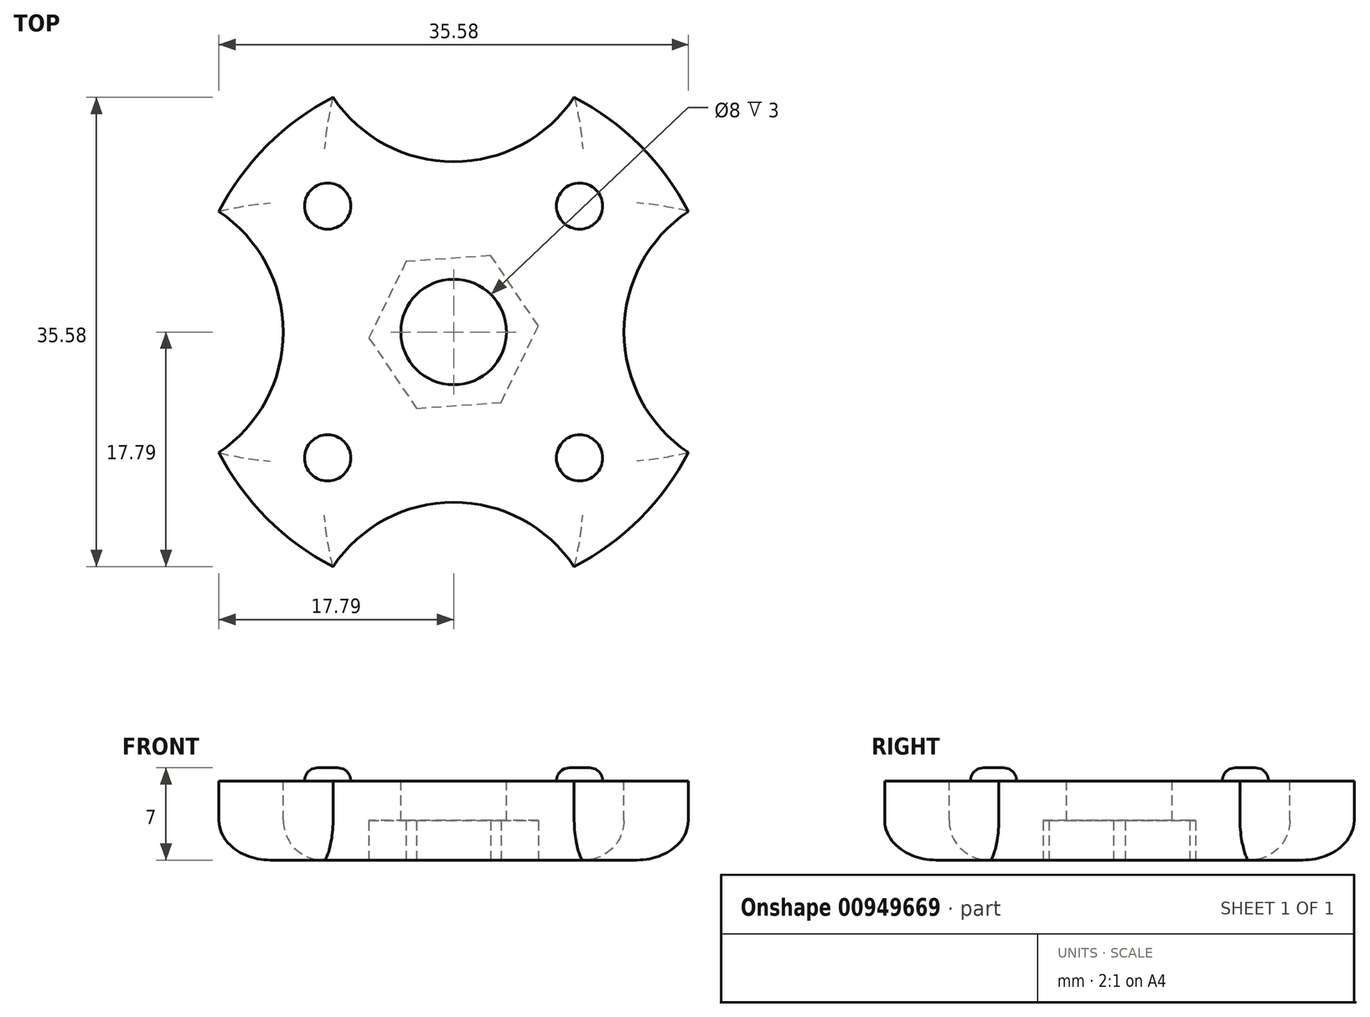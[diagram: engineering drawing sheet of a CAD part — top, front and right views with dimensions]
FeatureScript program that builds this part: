
annotation { "Feature Type Name" : "Feature", "Feature Type Description" : "" }
export const myFeature = defineFeature(function(context is Context, id is Id, definition is map)
    precondition{}
    {
        {
            var Q0;
            Q0=qCreatedBy(makeId("Top.planeOp"),FACE);
            var sketch = newSketch(context, id + "F0", { "sketchPlane" : qUnion([Q0])});
            skCircle(sketch, "E0", {"center": v(0, 0) * mm, "radius": 20 * mm});
            skCircle(sketch, "E1", {"center": v(0, 0) * mm, "radius": 13.5 * mm, "construction": true});
            skCircle(sketch, "E2", {"center": v(0, 13.5) * mm, "radius": 1.75 * mm});
            skCircle(sketch, "E3.1.0", {"center": v(-13.5, 0) * mm, "radius": 1.75 * mm});
            skCircle(sketch, "E3.2.0", {"center": v(0, -13.5) * mm, "radius": 1.75 * mm});
            skCircle(sketch, "E3.3.0", {"center": v(13.5, 0) * mm, "radius": 1.75 * mm});
            skCircle(sketch, "E4", {"center": v(0, 0) * mm, "radius": 4 * mm});
            skSolve(sketch);
        }
        {
            var Q0;
            Q0=makeQuery(id+"F0.imprint","IMPRINT",FACE,{"disambiguationData":[TD([[makeQuery(id+"F0.imprint","IMPRINT",EDGE,{"derivedFrom":sQuery(id+"F0.wireOp",EDGE,"E0")}),1.0]])]});
            extrude(context, id + "F1", {"entities" : qUnion([Q0]), "oppositeDirection" : true, "depth" : 6 * mm, "offsetDistance" : 25 * mm});
        }
        {
            var Q0;
            Q0=makeQuery(id+"F0.imprint","IMPRINT",FACE,{"disambiguationData":[TD([[makeQuery(id+"F0.imprint","IMPRINT",EDGE,{"derivedFrom":sQuery(id+"F0.wireOp",EDGE,"E3.1.0")}),1.0]])]});
            var Q1;
            Q1=makeQuery(id+"F0.imprint","IMPRINT",FACE,{"disambiguationData":[TD([[makeQuery(id+"F0.imprint","IMPRINT",EDGE,{"derivedFrom":sQuery(id+"F0.wireOp",EDGE,"E2")}),1.0]])]});
            var Q2;
            Q2=makeQuery(id+"F0.imprint","IMPRINT",FACE,{"disambiguationData":[TD([[makeQuery(id+"F0.imprint","IMPRINT",EDGE,{"derivedFrom":sQuery(id+"F0.wireOp",EDGE,"E3.3.0")}),1.0]])]});
            var Q3;
            Q3=makeQuery(id+"F0.imprint","IMPRINT",FACE,{"disambiguationData":[TD([[makeQuery(id+"F0.imprint","IMPRINT",EDGE,{"derivedFrom":sQuery(id+"F0.wireOp",EDGE,"E3.2.0")}),1.0]])]});
            extrude(context, id + "F2", {"entities" : qUnion([Q0, Q1, Q2, Q3]), "depth" : 1 * mm, "offsetDistance" : 25 * mm});
        }
        {
            var Q0;
            Q0=makeQuery(id+"F2.opExtrude","CAP_FACE",FACE,{"disambiguationData":[OSD([sQuery(id+"F0.wireOp",EDGE,"E3.2.0")])],"isStart":true});
            var Q1;
            Q1=makeQuery(id+"F1.opExtrude","CAP_FACE",FACE,{"disambiguationData":[OSD([sQuery(id+"F0.wireOp",EDGE,"E0"),sQuery(id+"F0.wireOp",EDGE,"E2"),sQuery(id+"F0.wireOp",EDGE,"E3.1.0"),sQuery(id+"F0.wireOp",EDGE,"E3.2.0"),sQuery(id+"F0.wireOp",EDGE,"E3.3.0"),sQuery(id+"F0.wireOp",EDGE,"E4")])],"isStart":false});
            extrude(context, id + "F3", {"entities" : qUnion([Q0]), "operationType" : NewBodyOperationType.ADD, "endBound" : BoundingType.UP_TO_SURFACE, "depth" : 25 * mm, "endBoundEntityFace" : qUnion([Q1]), "offsetDistance" : 25 * mm});
        }
        {
            var Q0;
            Q0=makeQuery(id+"F2.opExtrude","CAP_FACE",FACE,{"disambiguationData":[OSD([sQuery(id+"F0.wireOp",EDGE,"E3.3.0")])],"isStart":true});
            var Q1;
            {var subQ0=sQuery(id+"F0.wireOp",EDGE,"E3.2.0");Q1=makeQuery(id+"F3.boolean.opBoolean","MERGE",FACE,{"derivedFrom":[makeQuery(id+"F1.opExtrude","CAP_FACE",FACE,{"disambiguationData":[OSD([sQuery(id+"F0.wireOp",EDGE,"E0"),sQuery(id+"F0.wireOp",EDGE,"E2"),sQuery(id+"F0.wireOp",EDGE,"E3.1.0"),subQ0,sQuery(id+"F0.wireOp",EDGE,"E3.3.0"),sQuery(id+"F0.wireOp",EDGE,"E4")])],"isStart":false}),makeQuery(id+"F3.opExtrude","CAP_FACE",FACE,{"disambiguationData":[OSD([subQ0])],"isStart":false})]});}
            extrude(context, id + "F4", {"entities" : qUnion([Q0]), "operationType" : NewBodyOperationType.ADD, "endBound" : BoundingType.UP_TO_SURFACE, "depth" : 25 * mm, "endBoundEntityFace" : qUnion([Q1]), "offsetDistance" : 25 * mm});
        }
        {
            var Q0;
            Q0=makeQuery(id+"F2.opExtrude","CAP_FACE",FACE,{"disambiguationData":[OSD([sQuery(id+"F0.wireOp",EDGE,"E3.1.0")])],"isStart":true});
            var Q1;
            {var subQ0=sQuery(id+"F0.wireOp",EDGE,"E3.3.0");var subQ1=sQuery(id+"F0.wireOp",EDGE,"E3.2.0");Q1=makeQuery(id+"F4.boolean.opBoolean","MERGE",FACE,{"derivedFrom":[makeQuery(id+"F3.boolean.opBoolean","MERGE",FACE,{"derivedFrom":[makeQuery(id+"F1.opExtrude","CAP_FACE",FACE,{"disambiguationData":[OSD([sQuery(id+"F0.wireOp",EDGE,"E0"),sQuery(id+"F0.wireOp",EDGE,"E2"),sQuery(id+"F0.wireOp",EDGE,"E3.1.0"),subQ1,subQ0,sQuery(id+"F0.wireOp",EDGE,"E4")])],"isStart":false}),makeQuery(id+"F3.opExtrude","CAP_FACE",FACE,{"disambiguationData":[OSD([subQ1])],"isStart":false})]}),makeQuery(id+"F4.opExtrude","CAP_FACE",FACE,{"disambiguationData":[OSD([subQ0])],"isStart":false})]});}
            extrude(context, id + "F5", {"entities" : qUnion([Q0]), "operationType" : NewBodyOperationType.ADD, "endBound" : BoundingType.UP_TO_SURFACE, "depth" : 25 * mm, "endBoundEntityFace" : qUnion([Q1]), "offsetDistance" : 25 * mm});
        }
        {
            var Q0;
            Q0=makeQuery(id+"F2.opExtrude","CAP_FACE",FACE,{"disambiguationData":[OSD([sQuery(id+"F0.wireOp",EDGE,"E2")])],"isStart":true});
            var Q1;
            {var subQ0=sQuery(id+"F0.wireOp",EDGE,"E3.1.0");var subQ1=sQuery(id+"F0.wireOp",EDGE,"E3.3.0");var subQ2=sQuery(id+"F0.wireOp",EDGE,"E3.2.0");Q1=makeQuery(id+"F5.boolean.opBoolean","MERGE",FACE,{"derivedFrom":[makeQuery(id+"F4.boolean.opBoolean","MERGE",FACE,{"derivedFrom":[makeQuery(id+"F3.boolean.opBoolean","MERGE",FACE,{"derivedFrom":[makeQuery(id+"F1.opExtrude","CAP_FACE",FACE,{"disambiguationData":[OSD([sQuery(id+"F0.wireOp",EDGE,"E0"),sQuery(id+"F0.wireOp",EDGE,"E2"),subQ0,subQ2,subQ1,sQuery(id+"F0.wireOp",EDGE,"E4")])],"isStart":false}),makeQuery(id+"F3.opExtrude","CAP_FACE",FACE,{"disambiguationData":[OSD([subQ2])],"isStart":false})]}),makeQuery(id+"F4.opExtrude","CAP_FACE",FACE,{"disambiguationData":[OSD([subQ1])],"isStart":false})]}),makeQuery(id+"F5.opExtrude","CAP_FACE",FACE,{"disambiguationData":[OSD([subQ0])],"isStart":false})]});}
            extrude(context, id + "F6", {"entities" : qUnion([Q0]), "operationType" : NewBodyOperationType.ADD, "endBound" : BoundingType.UP_TO_SURFACE, "depth" : 25 * mm, "endBoundEntityFace" : qUnion([Q1]), "offsetDistance" : 25 * mm});
        }
        {
            var Q0;
            Q0=makeQuery(id+"F2.opExtrude","CAP_EDGE",EDGE,{"disambiguationData":[OSD([sQuery(id+"F0.wireOp",EDGE,"E3.3.0")])],"isStart":false});
            var Q1;
            Q1=makeQuery(id+"F2.opExtrude","CAP_EDGE",EDGE,{"disambiguationData":[OSD([sQuery(id+"F0.wireOp",EDGE,"E3.2.0")])],"isStart":false});
            var Q2;
            Q2=makeQuery(id+"F2.opExtrude","CAP_EDGE",EDGE,{"disambiguationData":[OSD([sQuery(id+"F0.wireOp",EDGE,"E2")])],"isStart":false});
            var Q3;
            Q3=makeQuery(id+"F2.opExtrude","CAP_EDGE",EDGE,{"disambiguationData":[OSD([sQuery(id+"F0.wireOp",EDGE,"E3.1.0")])],"isStart":false});
            fillet(context, id + "F7", {"entities" : qUnion([Q0, Q1, Q2, Q3]), "radius" : 1 * mm, "tangentPropagation" : true, "allowEdgeOverflow" : false});
        }
        {
            var Q0;
            {var subQ0=sQuery(id+"F0.wireOp",EDGE,"E2");var subQ1=sQuery(id+"F0.wireOp",EDGE,"E3.1.0");var subQ2=sQuery(id+"F0.wireOp",EDGE,"E3.3.0");var subQ3=sQuery(id+"F0.wireOp",EDGE,"E3.2.0");Q0=makeQuery(id+"F6.boolean.opBoolean","MERGE",FACE,{"derivedFrom":[makeQuery(id+"F5.boolean.opBoolean","MERGE",FACE,{"derivedFrom":[makeQuery(id+"F4.boolean.opBoolean","MERGE",FACE,{"derivedFrom":[makeQuery(id+"F3.boolean.opBoolean","MERGE",FACE,{"derivedFrom":[makeQuery(id+"F1.opExtrude","CAP_FACE",FACE,{"disambiguationData":[OSD([sQuery(id+"F0.wireOp",EDGE,"E0"),subQ0,subQ1,subQ3,subQ2,sQuery(id+"F0.wireOp",EDGE,"E4")])],"isStart":false}),makeQuery(id+"F3.opExtrude","CAP_FACE",FACE,{"disambiguationData":[OSD([subQ3])],"isStart":false})]}),makeQuery(id+"F4.opExtrude","CAP_FACE",FACE,{"disambiguationData":[OSD([subQ2])],"isStart":false})]}),makeQuery(id+"F5.opExtrude","CAP_FACE",FACE,{"disambiguationData":[OSD([subQ1])],"isStart":false})]}),makeQuery(id+"F6.opExtrude","CAP_FACE",FACE,{"disambiguationData":[OSD([subQ0])],"isStart":false})]});}
            var sketch = newSketch(context, id + "F8", { "sketchPlane" : qUnion([Q0])});
            skCircle(sketch, "E5.cCircle", {"center": v(0, 0) * mm, "radius": 6.44 * mm, "construction": true});
            skLineSegment(sketch, "E5.0", {"start": v(4.22, -4.86) * mm, "end": v(-2.1, -6.09) * mm});
            skLineSegment(sketch, "E5.1", {"start": v(-2.1, -6.09) * mm, "end": v(-6.32, -1.23) * mm});
            skLineSegment(sketch, "E5.2", {"start": v(-6.32, -1.23) * mm, "end": v(-4.22, 4.86) * mm});
            skLineSegment(sketch, "E5.3", {"start": v(-4.22, 4.86) * mm, "end": v(2.1, 6.09) * mm});
            skLineSegment(sketch, "E5.4", {"start": v(2.1, 6.09) * mm, "end": v(6.32, 1.23) * mm});
            skLineSegment(sketch, "E5.5", {"start": v(6.32, 1.23) * mm, "end": v(4.22, -4.86) * mm});
            skSolve(sketch);
        }
        {
            var Q0;
            Q0=makeQuery(id+"F8.imprint","IMPRINT",FACE,{"disambiguationData":[TD([[makeQuery(id+"F8.imprint","IMPRINT",EDGE,{"derivedFrom":sQuery(id+"F8.wireOp",EDGE,"E5.0")}),-1.0]])]});
            extrude(context, id + "F9", {"entities" : qUnion([Q0]), "operationType" : NewBodyOperationType.REMOVE, "oppositeDirection" : true, "depth" : 3 * mm, "offsetDistance" : 25 * mm});
        }
        {
            var Q0;
            Q0=makeQuery(id+"F1.opExtrude","SWEPT_BODY",BODY,{"disambiguationData":[OSD([sQuery(id+"F0.wireOp",EDGE,"E0"),sQuery(id+"F0.wireOp",EDGE,"E2"),sQuery(id+"F0.wireOp",EDGE,"E3.1.0"),sQuery(id+"F0.wireOp",EDGE,"E3.2.0"),sQuery(id+"F0.wireOp",EDGE,"E3.3.0"),sQuery(id+"F0.wireOp",EDGE,"E4")])]});
            var Q1;
            Q1=makeQuery(id+"F1.opExtrude","SWEPT_FACE",FACE,{"disambiguationData":[OSD([sQuery(id+"F0.wireOp",EDGE,"E4")])]});
            transform(context, id + "F10", {"entities" : qUnion([Q0]), "transformType" : TransformType.ROTATION, "transformAxis" : qUnion([Q1]), "angle" : 45 * degree, "makeCopy" : false});
        }
        {
            var Q0;
            Q0=makeQuery(id+"F1.opExtrude","CAP_FACE",FACE,{"disambiguationData":[OSD([sQuery(id+"F0.wireOp",EDGE,"E0"),sQuery(id+"F0.wireOp",EDGE,"E2"),sQuery(id+"F0.wireOp",EDGE,"E3.1.0"),sQuery(id+"F0.wireOp",EDGE,"E3.2.0"),sQuery(id+"F0.wireOp",EDGE,"E3.3.0"),sQuery(id+"F0.wireOp",EDGE,"E4")])],"isStart":true});
            var sketch = newSketch(context, id + "F11", { "sketchPlane" : qUnion([Q0])});
            skCircle(sketch, "E6", {"center": v(0, 0) * mm, "radius": 23.91 * mm, "construction": true});
            skCircle(sketch, "E7", {"center": v(0, 23.91) * mm, "radius": 11 * mm});
            skCircle(sketch, "E8.1.0", {"center": v(-23.91, 0) * mm, "radius": 11 * mm});
            skCircle(sketch, "E8.2.0", {"center": v(0, -23.91) * mm, "radius": 11 * mm});
            skCircle(sketch, "E8.3.0", {"center": v(23.91, 0) * mm, "radius": 11 * mm});
            skSolve(sketch);
        }
        {
            var Q0;
            {var subQ0=sQuery(id+"F11.wireOp",EDGE,"E7");var subQ1=makeQuery(id+"F1.opExtrude","CAP_EDGE",EDGE,{"disambiguationData":[OSD([sQuery(id+"F0.wireOp",EDGE,"E0")])],"isStart":true});var subQ2=makeQuery(id+"F11.imprint","INTERSECT",VERTEX,{"disambiguationData":[OD(0.0)],"derivedFrom":[subQ1,subQ0]});Q0=makeQuery(id+"F11.imprint","IMPRINT",FACE,{"disambiguationData":[TD([[makeQuery(id+"F11.imprint","IMPRINT",EDGE,{"disambiguationData":[TD([[subQ2,-1.0]])],"derivedFrom":subQ0}),1.0]])]});}
            var Q1;
            {var subQ0=sQuery(id+"F11.wireOp",EDGE,"E8.3.0");var subQ1=makeQuery(id+"F1.opExtrude","CAP_EDGE",EDGE,{"disambiguationData":[OSD([sQuery(id+"F0.wireOp",EDGE,"E0")])],"isStart":true});var subQ2=makeQuery(id+"F11.imprint","INTERSECT",VERTEX,{"disambiguationData":[OD(0.0)],"derivedFrom":[subQ1,subQ0]});Q1=makeQuery(id+"F11.imprint","IMPRINT",FACE,{"disambiguationData":[TD([[makeQuery(id+"F11.imprint","IMPRINT",EDGE,{"disambiguationData":[TD([[subQ2,1.0]])],"derivedFrom":subQ0}),1.0]])]});}
            var Q2;
            {var subQ0=sQuery(id+"F11.wireOp",EDGE,"E8.2.0");var subQ1=makeQuery(id+"F1.opExtrude","CAP_EDGE",EDGE,{"disambiguationData":[OSD([sQuery(id+"F0.wireOp",EDGE,"E0")])],"isStart":true});var subQ2=makeQuery(id+"F11.imprint","INTERSECT",VERTEX,{"disambiguationData":[OD(0.0)],"derivedFrom":[subQ1,subQ0]});Q2=makeQuery(id+"F11.imprint","IMPRINT",FACE,{"disambiguationData":[TD([[makeQuery(id+"F11.imprint","IMPRINT",EDGE,{"disambiguationData":[TD([[subQ2,1.0]])],"derivedFrom":subQ0}),1.0]])]});}
            var Q3;
            {var subQ0=sQuery(id+"F11.wireOp",EDGE,"E8.1.0");var subQ1=makeQuery(id+"F1.opExtrude","CAP_EDGE",EDGE,{"disambiguationData":[OSD([sQuery(id+"F0.wireOp",EDGE,"E0")])],"isStart":true});var subQ2=makeQuery(id+"F11.imprint","INTERSECT",VERTEX,{"disambiguationData":[OD(0.0)],"derivedFrom":[subQ1,subQ0]});Q3=makeQuery(id+"F11.imprint","IMPRINT",FACE,{"disambiguationData":[TD([[makeQuery(id+"F11.imprint","IMPRINT",EDGE,{"disambiguationData":[TD([[subQ2,-1.0]])],"derivedFrom":subQ0}),1.0]])]});}
            var Q4;
            {var subQ0=sQuery(id+"F11.wireOp",EDGE,"E8.1.0");var subQ1=makeQuery(id+"F1.opExtrude","CAP_EDGE",EDGE,{"disambiguationData":[OSD([sQuery(id+"F0.wireOp",EDGE,"E0")])],"isStart":true});var subQ2=makeQuery(id+"F11.imprint","INTERSECT",VERTEX,{"disambiguationData":[OD(0.0)],"derivedFrom":[subQ1,subQ0]});Q4=makeQuery(id+"F11.imprint","IMPRINT",FACE,{"disambiguationData":[TD([[makeQuery(id+"F11.imprint","IMPRINT",EDGE,{"disambiguationData":[TD([[subQ2,1.0]])],"derivedFrom":subQ0}),1.0]])]});}
            var Q5;
            {var subQ0=sQuery(id+"F11.wireOp",EDGE,"E7");var subQ1=makeQuery(id+"F1.opExtrude","CAP_EDGE",EDGE,{"disambiguationData":[OSD([sQuery(id+"F0.wireOp",EDGE,"E0")])],"isStart":true});var subQ2=makeQuery(id+"F11.imprint","INTERSECT",VERTEX,{"disambiguationData":[OD(0.0)],"derivedFrom":[subQ1,subQ0]});Q5=makeQuery(id+"F11.imprint","IMPRINT",FACE,{"disambiguationData":[TD([[makeQuery(id+"F11.imprint","IMPRINT",EDGE,{"disambiguationData":[TD([[subQ2,1.0]])],"derivedFrom":subQ0}),1.0]])]});}
            var Q6;
            {var subQ0=sQuery(id+"F11.wireOp",EDGE,"E8.3.0");var subQ1=makeQuery(id+"F1.opExtrude","CAP_EDGE",EDGE,{"disambiguationData":[OSD([sQuery(id+"F0.wireOp",EDGE,"E0")])],"isStart":true});var subQ2=makeQuery(id+"F11.imprint","INTERSECT",VERTEX,{"disambiguationData":[OD(0.0)],"derivedFrom":[subQ1,subQ0]});Q6=makeQuery(id+"F11.imprint","IMPRINT",FACE,{"disambiguationData":[TD([[makeQuery(id+"F11.imprint","IMPRINT",EDGE,{"disambiguationData":[TD([[subQ2,-1.0]])],"derivedFrom":subQ0}),1.0]])]});}
            var Q7;
            {var subQ0=sQuery(id+"F11.wireOp",EDGE,"E8.2.0");var subQ1=makeQuery(id+"F1.opExtrude","CAP_EDGE",EDGE,{"disambiguationData":[OSD([sQuery(id+"F0.wireOp",EDGE,"E0")])],"isStart":true});var subQ2=makeQuery(id+"F11.imprint","INTERSECT",VERTEX,{"disambiguationData":[OD(0.0)],"derivedFrom":[subQ1,subQ0]});Q7=makeQuery(id+"F11.imprint","IMPRINT",FACE,{"disambiguationData":[TD([[makeQuery(id+"F11.imprint","IMPRINT",EDGE,{"disambiguationData":[TD([[subQ2,-1.0]])],"derivedFrom":subQ0}),1.0]])]});}
            extrude(context, id + "F12", {"entities" : qUnion([Q0, Q1, Q2, Q3, Q4, Q5, Q6, Q7]), "operationType" : NewBodyOperationType.REMOVE, "endBound" : BoundingType.THROUGH_ALL, "oppositeDirection" : true, "depth" : 25 * mm, "offsetDistance" : 25 * mm});
        }
        {
            var Q0;
            {var subQ0=sQuery(id+"F0.wireOp",EDGE,"E2");var subQ1=sQuery(id+"F0.wireOp",EDGE,"E3.1.0");var subQ2=sQuery(id+"F0.wireOp",EDGE,"E3.3.0");var subQ3=sQuery(id+"F0.wireOp",EDGE,"E3.2.0");Q0=makeQuery(id+"F12.boolean.opBoolean","INTERSECT",EDGE,{"derivedFrom":[makeQuery(id+"F6.boolean.opBoolean","MERGE",FACE,{"derivedFrom":[makeQuery(id+"F5.boolean.opBoolean","MERGE",FACE,{"derivedFrom":[makeQuery(id+"F4.boolean.opBoolean","MERGE",FACE,{"derivedFrom":[makeQuery(id+"F3.boolean.opBoolean","MERGE",FACE,{"derivedFrom":[makeQuery(id+"F1.opExtrude","CAP_FACE",FACE,{"disambiguationData":[OSD([sQuery(id+"F0.wireOp",EDGE,"E0"),subQ0,subQ1,subQ3,subQ2,sQuery(id+"F0.wireOp",EDGE,"E4")])],"isStart":false}),makeQuery(id+"F3.opExtrude","CAP_FACE",FACE,{"disambiguationData":[OSD([subQ3])],"isStart":false})]}),makeQuery(id+"F4.opExtrude","CAP_FACE",FACE,{"disambiguationData":[OSD([subQ2])],"isStart":false})]}),makeQuery(id+"F5.opExtrude","CAP_FACE",FACE,{"disambiguationData":[OSD([subQ1])],"isStart":false})]}),makeQuery(id+"F6.opExtrude","CAP_FACE",FACE,{"disambiguationData":[OSD([subQ0])],"isStart":false})]}),makeQuery(id+"F12.opExtrude","SWEPT_FACE",FACE,{"disambiguationData":[OSD([sQuery(id+"F11.wireOp",EDGE,"E8.1.0")])]})]});}
            var Q1;
            {var subQ0=sQuery(id+"F0.wireOp",EDGE,"E3.3.0");var subQ1=sQuery(id+"F0.wireOp",EDGE,"E3.2.0");var subQ2=sQuery(id+"F0.wireOp",EDGE,"E3.1.0");var subQ3=sQuery(id+"F0.wireOp",EDGE,"E2");var subQ4=sQuery(id+"F0.wireOp",EDGE,"E0");Q1=makeQuery(id+"F12.boolean.opBoolean","SPLIT",EDGE,{"disambiguationData":[TD([makeQuery(id+"F1.opExtrude","SWEPT_FACE",FACE,{"disambiguationData":[OSD([subQ4])]}),makeQuery(id+"F1.opExtrude","CAP_FACE",FACE,{"disambiguationData":[OSD([subQ4,subQ3,subQ2,subQ1,subQ0,sQuery(id+"F0.wireOp",EDGE,"E4")])],"isStart":false}),makeQuery(id+"F3.opExtrude","CAP_FACE",FACE,{"disambiguationData":[OSD([subQ1])],"isStart":false}),makeQuery(id+"F4.opExtrude","CAP_FACE",FACE,{"disambiguationData":[OSD([subQ0])],"isStart":false}),makeQuery(id+"F5.opExtrude","CAP_FACE",FACE,{"disambiguationData":[OSD([subQ2])],"isStart":false}),makeQuery(id+"F6.opExtrude","CAP_FACE",FACE,{"disambiguationData":[OSD([subQ3])],"isStart":false}),makeQuery(id+"F12.opExtrude","SWEPT_FACE",FACE,{"disambiguationData":[OSD([sQuery(id+"F11.wireOp",EDGE,"E8.1.0")])]}),makeQuery(id+"F12.opExtrude","SWEPT_FACE",FACE,{"disambiguationData":[OSD([sQuery(id+"F11.wireOp",EDGE,"E8.2.0")])]})])],"derivedFrom":makeQuery(id+"F1.opExtrude","CAP_EDGE",EDGE,{"disambiguationData":[OSD([subQ4])],"isStart":false})});}
            var Q2;
            {var subQ0=sQuery(id+"F0.wireOp",EDGE,"E2");var subQ1=sQuery(id+"F0.wireOp",EDGE,"E3.1.0");var subQ2=sQuery(id+"F0.wireOp",EDGE,"E3.3.0");var subQ3=sQuery(id+"F0.wireOp",EDGE,"E3.2.0");Q2=makeQuery(id+"F12.boolean.opBoolean","INTERSECT",EDGE,{"derivedFrom":[makeQuery(id+"F6.boolean.opBoolean","MERGE",FACE,{"derivedFrom":[makeQuery(id+"F5.boolean.opBoolean","MERGE",FACE,{"derivedFrom":[makeQuery(id+"F4.boolean.opBoolean","MERGE",FACE,{"derivedFrom":[makeQuery(id+"F3.boolean.opBoolean","MERGE",FACE,{"derivedFrom":[makeQuery(id+"F1.opExtrude","CAP_FACE",FACE,{"disambiguationData":[OSD([sQuery(id+"F0.wireOp",EDGE,"E0"),subQ0,subQ1,subQ3,subQ2,sQuery(id+"F0.wireOp",EDGE,"E4")])],"isStart":false}),makeQuery(id+"F3.opExtrude","CAP_FACE",FACE,{"disambiguationData":[OSD([subQ3])],"isStart":false})]}),makeQuery(id+"F4.opExtrude","CAP_FACE",FACE,{"disambiguationData":[OSD([subQ2])],"isStart":false})]}),makeQuery(id+"F5.opExtrude","CAP_FACE",FACE,{"disambiguationData":[OSD([subQ1])],"isStart":false})]}),makeQuery(id+"F6.opExtrude","CAP_FACE",FACE,{"disambiguationData":[OSD([subQ0])],"isStart":false})]}),makeQuery(id+"F12.opExtrude","SWEPT_FACE",FACE,{"disambiguationData":[OSD([sQuery(id+"F11.wireOp",EDGE,"E8.2.0")])]})]});}
            var Q3;
            {var subQ0=sQuery(id+"F0.wireOp",EDGE,"E3.3.0");var subQ1=sQuery(id+"F0.wireOp",EDGE,"E3.2.0");var subQ2=sQuery(id+"F0.wireOp",EDGE,"E3.1.0");var subQ3=sQuery(id+"F0.wireOp",EDGE,"E2");var subQ4=sQuery(id+"F0.wireOp",EDGE,"E0");Q3=makeQuery(id+"F12.boolean.opBoolean","SPLIT",EDGE,{"disambiguationData":[TD([makeQuery(id+"F1.opExtrude","SWEPT_FACE",FACE,{"disambiguationData":[OSD([subQ4])]}),makeQuery(id+"F1.opExtrude","CAP_FACE",FACE,{"disambiguationData":[OSD([subQ4,subQ3,subQ2,subQ1,subQ0,sQuery(id+"F0.wireOp",EDGE,"E4")])],"isStart":false}),makeQuery(id+"F3.opExtrude","CAP_FACE",FACE,{"disambiguationData":[OSD([subQ1])],"isStart":false}),makeQuery(id+"F4.opExtrude","CAP_FACE",FACE,{"disambiguationData":[OSD([subQ0])],"isStart":false}),makeQuery(id+"F5.opExtrude","CAP_FACE",FACE,{"disambiguationData":[OSD([subQ2])],"isStart":false}),makeQuery(id+"F6.opExtrude","CAP_FACE",FACE,{"disambiguationData":[OSD([subQ3])],"isStart":false}),makeQuery(id+"F12.opExtrude","SWEPT_FACE",FACE,{"disambiguationData":[OSD([sQuery(id+"F11.wireOp",EDGE,"E8.2.0")])]}),makeQuery(id+"F12.opExtrude","SWEPT_FACE",FACE,{"disambiguationData":[OSD([sQuery(id+"F11.wireOp",EDGE,"E8.3.0")])]})])],"derivedFrom":makeQuery(id+"F1.opExtrude","CAP_EDGE",EDGE,{"disambiguationData":[OSD([subQ4])],"isStart":false})});}
            var Q4;
            {var subQ0=sQuery(id+"F0.wireOp",EDGE,"E2");var subQ1=sQuery(id+"F0.wireOp",EDGE,"E3.1.0");var subQ2=sQuery(id+"F0.wireOp",EDGE,"E3.3.0");var subQ3=sQuery(id+"F0.wireOp",EDGE,"E3.2.0");Q4=makeQuery(id+"F12.boolean.opBoolean","INTERSECT",EDGE,{"derivedFrom":[makeQuery(id+"F6.boolean.opBoolean","MERGE",FACE,{"derivedFrom":[makeQuery(id+"F5.boolean.opBoolean","MERGE",FACE,{"derivedFrom":[makeQuery(id+"F4.boolean.opBoolean","MERGE",FACE,{"derivedFrom":[makeQuery(id+"F3.boolean.opBoolean","MERGE",FACE,{"derivedFrom":[makeQuery(id+"F1.opExtrude","CAP_FACE",FACE,{"disambiguationData":[OSD([sQuery(id+"F0.wireOp",EDGE,"E0"),subQ0,subQ1,subQ3,subQ2,sQuery(id+"F0.wireOp",EDGE,"E4")])],"isStart":false}),makeQuery(id+"F3.opExtrude","CAP_FACE",FACE,{"disambiguationData":[OSD([subQ3])],"isStart":false})]}),makeQuery(id+"F4.opExtrude","CAP_FACE",FACE,{"disambiguationData":[OSD([subQ2])],"isStart":false})]}),makeQuery(id+"F5.opExtrude","CAP_FACE",FACE,{"disambiguationData":[OSD([subQ1])],"isStart":false})]}),makeQuery(id+"F6.opExtrude","CAP_FACE",FACE,{"disambiguationData":[OSD([subQ0])],"isStart":false})]}),makeQuery(id+"F12.opExtrude","SWEPT_FACE",FACE,{"disambiguationData":[OSD([sQuery(id+"F11.wireOp",EDGE,"E8.3.0")])]})]});}
            var Q5;
            {var subQ0=sQuery(id+"F0.wireOp",EDGE,"E3.3.0");var subQ1=sQuery(id+"F0.wireOp",EDGE,"E3.2.0");var subQ2=sQuery(id+"F0.wireOp",EDGE,"E3.1.0");var subQ3=sQuery(id+"F0.wireOp",EDGE,"E2");var subQ4=sQuery(id+"F0.wireOp",EDGE,"E0");Q5=makeQuery(id+"F12.boolean.opBoolean","SPLIT",EDGE,{"disambiguationData":[TD([makeQuery(id+"F1.opExtrude","SWEPT_FACE",FACE,{"disambiguationData":[OSD([subQ4])]}),makeQuery(id+"F1.opExtrude","CAP_FACE",FACE,{"disambiguationData":[OSD([subQ4,subQ3,subQ2,subQ1,subQ0,sQuery(id+"F0.wireOp",EDGE,"E4")])],"isStart":false}),makeQuery(id+"F3.opExtrude","CAP_FACE",FACE,{"disambiguationData":[OSD([subQ1])],"isStart":false}),makeQuery(id+"F4.opExtrude","CAP_FACE",FACE,{"disambiguationData":[OSD([subQ0])],"isStart":false}),makeQuery(id+"F5.opExtrude","CAP_FACE",FACE,{"disambiguationData":[OSD([subQ2])],"isStart":false}),makeQuery(id+"F6.opExtrude","CAP_FACE",FACE,{"disambiguationData":[OSD([subQ3])],"isStart":false}),makeQuery(id+"F12.opExtrude","SWEPT_FACE",FACE,{"disambiguationData":[OSD([sQuery(id+"F11.wireOp",EDGE,"E7")])]}),makeQuery(id+"F12.opExtrude","SWEPT_FACE",FACE,{"disambiguationData":[OSD([sQuery(id+"F11.wireOp",EDGE,"E8.3.0")])]})])],"derivedFrom":makeQuery(id+"F1.opExtrude","CAP_EDGE",EDGE,{"disambiguationData":[OSD([subQ4])],"isStart":false})});}
            var Q6;
            {var subQ0=sQuery(id+"F0.wireOp",EDGE,"E2");var subQ1=sQuery(id+"F0.wireOp",EDGE,"E3.1.0");var subQ2=sQuery(id+"F0.wireOp",EDGE,"E3.3.0");var subQ3=sQuery(id+"F0.wireOp",EDGE,"E3.2.0");Q6=makeQuery(id+"F12.boolean.opBoolean","INTERSECT",EDGE,{"derivedFrom":[makeQuery(id+"F6.boolean.opBoolean","MERGE",FACE,{"derivedFrom":[makeQuery(id+"F5.boolean.opBoolean","MERGE",FACE,{"derivedFrom":[makeQuery(id+"F4.boolean.opBoolean","MERGE",FACE,{"derivedFrom":[makeQuery(id+"F3.boolean.opBoolean","MERGE",FACE,{"derivedFrom":[makeQuery(id+"F1.opExtrude","CAP_FACE",FACE,{"disambiguationData":[OSD([sQuery(id+"F0.wireOp",EDGE,"E0"),subQ0,subQ1,subQ3,subQ2,sQuery(id+"F0.wireOp",EDGE,"E4")])],"isStart":false}),makeQuery(id+"F3.opExtrude","CAP_FACE",FACE,{"disambiguationData":[OSD([subQ3])],"isStart":false})]}),makeQuery(id+"F4.opExtrude","CAP_FACE",FACE,{"disambiguationData":[OSD([subQ2])],"isStart":false})]}),makeQuery(id+"F5.opExtrude","CAP_FACE",FACE,{"disambiguationData":[OSD([subQ1])],"isStart":false})]}),makeQuery(id+"F6.opExtrude","CAP_FACE",FACE,{"disambiguationData":[OSD([subQ0])],"isStart":false})]}),makeQuery(id+"F12.opExtrude","SWEPT_FACE",FACE,{"disambiguationData":[OSD([sQuery(id+"F11.wireOp",EDGE,"E7")])]})]});}
            var Q7;
            {var subQ0=sQuery(id+"F0.wireOp",EDGE,"E3.3.0");var subQ1=sQuery(id+"F0.wireOp",EDGE,"E3.2.0");var subQ2=sQuery(id+"F0.wireOp",EDGE,"E3.1.0");var subQ3=sQuery(id+"F0.wireOp",EDGE,"E2");var subQ4=sQuery(id+"F0.wireOp",EDGE,"E0");Q7=makeQuery(id+"F12.boolean.opBoolean","SPLIT",EDGE,{"disambiguationData":[TD([makeQuery(id+"F1.opExtrude","SWEPT_FACE",FACE,{"disambiguationData":[OSD([subQ4])]}),makeQuery(id+"F1.opExtrude","CAP_FACE",FACE,{"disambiguationData":[OSD([subQ4,subQ3,subQ2,subQ1,subQ0,sQuery(id+"F0.wireOp",EDGE,"E4")])],"isStart":false}),makeQuery(id+"F3.opExtrude","CAP_FACE",FACE,{"disambiguationData":[OSD([subQ1])],"isStart":false}),makeQuery(id+"F4.opExtrude","CAP_FACE",FACE,{"disambiguationData":[OSD([subQ0])],"isStart":false}),makeQuery(id+"F5.opExtrude","CAP_FACE",FACE,{"disambiguationData":[OSD([subQ2])],"isStart":false}),makeQuery(id+"F6.opExtrude","CAP_FACE",FACE,{"disambiguationData":[OSD([subQ3])],"isStart":false}),makeQuery(id+"F12.opExtrude","SWEPT_FACE",FACE,{"disambiguationData":[OSD([sQuery(id+"F11.wireOp",EDGE,"E7")])]}),makeQuery(id+"F12.opExtrude","SWEPT_FACE",FACE,{"disambiguationData":[OSD([sQuery(id+"F11.wireOp",EDGE,"E8.1.0")])]})])],"derivedFrom":makeQuery(id+"F1.opExtrude","CAP_EDGE",EDGE,{"disambiguationData":[OSD([subQ4])],"isStart":false})});}
            fillet(context, id + "F13", {"entities" : qUnion([Q0, Q1, Q2, Q3, Q4, Q5, Q6, Q7]), "radius" : 3 * mm, "tangentPropagation" : true, "allowEdgeOverflow" : false});
        }
    });
